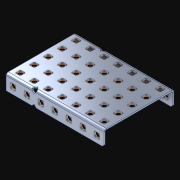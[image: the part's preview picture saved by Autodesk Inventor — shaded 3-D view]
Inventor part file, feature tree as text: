
AUTODESK INVENTOR PART (.ipt)
format: ipt  version: 2021 (Build 250183000, 183)  size: 1,550,336 bytes
history: native  units: in
note: dims shown in document units (in); Inventor stores cm internally (conversion verified against a paired STEP export)
features: extrude x50, other x50, sketch x4, pattern_linear x3
ambient origin geometry x8: Origin, YZ Plane, XZ Plane, XY Plane, X Axis, Y Axis, Z Axis, Center Point
bodies: Solid1 (feature_tree)
feature tree (107):
  pattern_linear  "Rectangular Pattern1"  Spacing1=0.182in  [1 undecoded]
  pattern_linear  "Rectangular Pattern2"  Spacing1=0.046in  [1 undecoded]
  pattern_linear  "Rectangular Pattern3"  Spacing1=0.5in  [1 undecoded]
  extrude  "Extrusion1"  Depth=0.046in
  sketch  "Sketch1"  dims[d0=0.182in]
  other  "Srf1"
  sketch  "Sketch2"  dims[d1=0.046in d2=0.0in]
  other  "Srf2"
  sketch  "Sketch3"  dims[d3=0.182in]
  other  "Srf3"
  other  "Srf4"
  other  "Srf5"
  other  "Srf6"
  other  "Srf7"
  other  "Srf8"
  other  "Srf9"
  other  "Srf38"
  other  "Srf39"
  other  "Srf40"
  other  "Srf41"
  other  "Srf42"
  other  "Srf43"
  other  "Srf72"
  other  "Srf73"
  other  "Srf74"
  other  "Srf75"
  other  "Srf76"
  other  "Srf77"
  other  "Srf78"
  other  "Srf107"
  other  "Srf108"
  other  "Srf109"
  other  "Srf110"
  other  "Srf111"
  other  "Srf112"
  other  "Srf113"
  other  "Srf142"
  other  "Srf143"
  other  "Srf144"
  other  "Srf145"
  other  "Srf146"
  other  "Srf147"
  other  "Srf148"
  other  "Srf177"
  other  "Srf178"
  other  "Srf179"
  other  "Srf180"
  other  "Srf181"
  other  "Srf182"
  other  "Srf183"
  other  "Srf212"
  other  "Srf213"
  other  "Srf214"
  other  "Srf215"
  other  "Srf216"
  other  "Srf217"
  sketch  "Sketch4"  dims[d4=0.046in d5=0.0in d6=0.182in d7=0.046in d8=0.0in d11=0.5in d12=2.7559in d14=0.5in d15=1.9685in d17=0.5in d18=2.7559in d20=0.5in d21=14.0in d22=0.0in]
  parser-record x1  (decoder bookkeeping rows leaked as tree rows — omitted from the tree; the rows remain in map.json)
  extrude  "ExtrusionSrf1"  Depth=0.046in
  extrude  "ExtrusionSrf2"  Depth=0.046in
  extrude  "ExtrusionSrf3"  Depth=0.046in
  extrude  "ExtrusionSrf4"  Depth=0.046in
  extrude  "ExtrusionSrf5"  Depth=0.046in
  extrude  "ExtrusionSrf6"  TaperAngle=0.0deg  [1 undecoded]
  extrude  "ExtrusionSrf7"  [1 undecoded]
  extrude  "ExtrusionSrf8"  [1 undecoded]
  extrude  "ExtrusionSrf9"  [1 undecoded]
  extrude  "ExtrusionSrf38"  [1 undecoded]
  extrude  "ExtrusionSrf39"  [1 undecoded]
  extrude  "ExtrusionSrf40"  [1 undecoded]
  extrude  "ExtrusionSrf41"  [1 undecoded]
  extrude  "ExtrusionSrf42"  [1 undecoded]
  extrude  "ExtrusionSrf43"  [1 undecoded]
  extrude  "ExtrusionSrf72"  [1 undecoded]
  extrude  "ExtrusionSrf73"  [1 undecoded]
  extrude  "ExtrusionSrf74"  [1 undecoded]
  extrude  "ExtrusionSrf75"  [1 undecoded]
  extrude  "ExtrusionSrf76"  [1 undecoded]
  extrude  "ExtrusionSrf77"  [1 undecoded]
  extrude  "ExtrusionSrf78"  [1 undecoded]
  extrude  "ExtrusionSrf107"  [1 undecoded]
  extrude  "ExtrusionSrf108"  [1 undecoded]
  extrude  "ExtrusionSrf109"  [1 undecoded]
  extrude  "ExtrusionSrf110"  [1 undecoded]
  extrude  "ExtrusionSrf111"  [1 undecoded]
  extrude  "ExtrusionSrf112"  [1 undecoded]
  extrude  "ExtrusionSrf113"  [1 undecoded]
  extrude  "ExtrusionSrf142"  [1 undecoded]
  extrude  "ExtrusionSrf143"  [1 undecoded]
  extrude  "ExtrusionSrf144"  [1 undecoded]
  extrude  "ExtrusionSrf145"  [1 undecoded]
  extrude  "ExtrusionSrf146"  [1 undecoded]
  extrude  "ExtrusionSrf147"  [1 undecoded]
  extrude  "ExtrusionSrf148"  [1 undecoded]
  extrude  "ExtrusionSrf177"  [1 undecoded]
  extrude  "ExtrusionSrf178"  [1 undecoded]
  extrude  "ExtrusionSrf179"  [1 undecoded]
  extrude  "ExtrusionSrf180"  [1 undecoded]
  extrude  "ExtrusionSrf181"  [1 undecoded]
  extrude  "ExtrusionSrf182"  [1 undecoded]
  extrude  "ExtrusionSrf183"  [1 undecoded]
  extrude  "ExtrusionSrf212"  [1 undecoded]
  extrude  "ExtrusionSrf213"  [1 undecoded]
  extrude  "ExtrusionSrf214"  [1 undecoded]
  extrude  "ExtrusionSrf215"  [1 undecoded]
  extrude  "ExtrusionSrf216"  [1 undecoded]
  extrude  "ExtrusionSrf217"  [1 undecoded]
note: 47 required parameter values undecoded (feature->parameter linkage not recoverable at this tier; creation-order binding heuristic only, values carry confidence <= 0.55)
